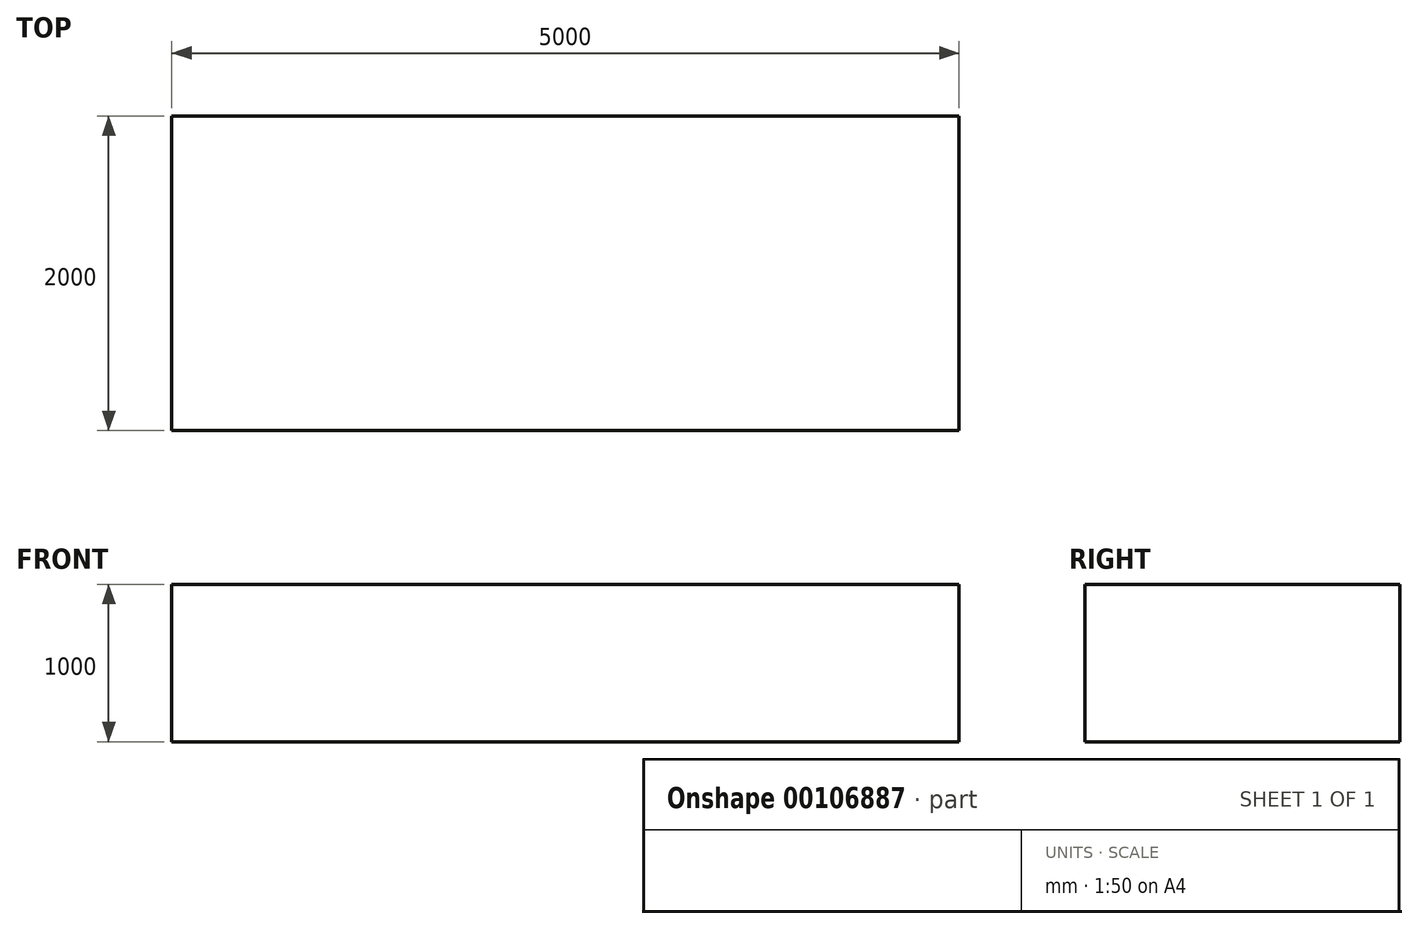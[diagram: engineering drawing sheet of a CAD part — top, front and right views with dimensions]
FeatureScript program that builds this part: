
annotation { "Feature Type Name" : "Feature", "Feature Type Description" : "" }
export const myFeature = defineFeature(function(context is Context, id is Id, definition is map)
    precondition{}
    {
        {
            var Q0;
            Q0=qCreatedBy(makeId("Front.planeOp"),FACE);
            var sketch = newSketch(context, id + "F0", { "sketchPlane" : qUnion([Q0])});
            skLineSegment(sketch, "E0.bottom", {"start": v(-2502.51, -244.44) * mm, "end": v(2497.49, -244.44) * mm});
            skLineSegment(sketch, "E0.top", {"start": v(-2502.51, -1244.44) * mm, "end": v(2497.49, -1244.44) * mm});
            skLineSegment(sketch, "E0.left", {"start": v(-2502.51, -244.44) * mm, "end": v(-2502.51, -1244.44) * mm});
            skLineSegment(sketch, "E0.right", {"start": v(2497.49, -244.44) * mm, "end": v(2497.49, -1244.44) * mm});
            skSolve(sketch);
        }
        {
            var Q0;
            Q0 = qSketchRegion(id + "F0", true);
            extrude(context, id + "F1", {"entities" : qUnion([Q0]), "depth" : 2000 * mm});
        }
        {
            var Q0;
            Q0=makeQuery(id+"F1.opExtrude","SWEPT_BODY",BODY,{"disambiguationData":[OSD([sQuery(id+"F0.wireOp",EDGE,"E0.bottom"),sQuery(id+"F0.wireOp",EDGE,"E0.top"),sQuery(id+"F0.wireOp",EDGE,"E0.left"),sQuery(id+"F0.wireOp",EDGE,"E0.right")])]});
            var Q1;
            Q1=makeQuery(id+"F1.opExtrude","CAP_VERTEX",VERTEX,{"disambiguationData":[OSD([sQuery(id+"F0.wireOp",EDGE,"E0.top"),sQuery(id+"F0.wireOp",EDGE,"E0.left")])],"isStart":false});
            var Q2;
            Q2=qCreatedBy(makeId("Origin.pointOp"),VERTEX);
            transform(context, id + "F2", {"entities" : qUnion([Q0]), "transformType" : TransformType.TRANSLATION_ENTITY, "oppositeDirectionEntity" : false, "transformLine" : qUnion([Q1, Q2]), "makeCopy" : false});
        }
    });
